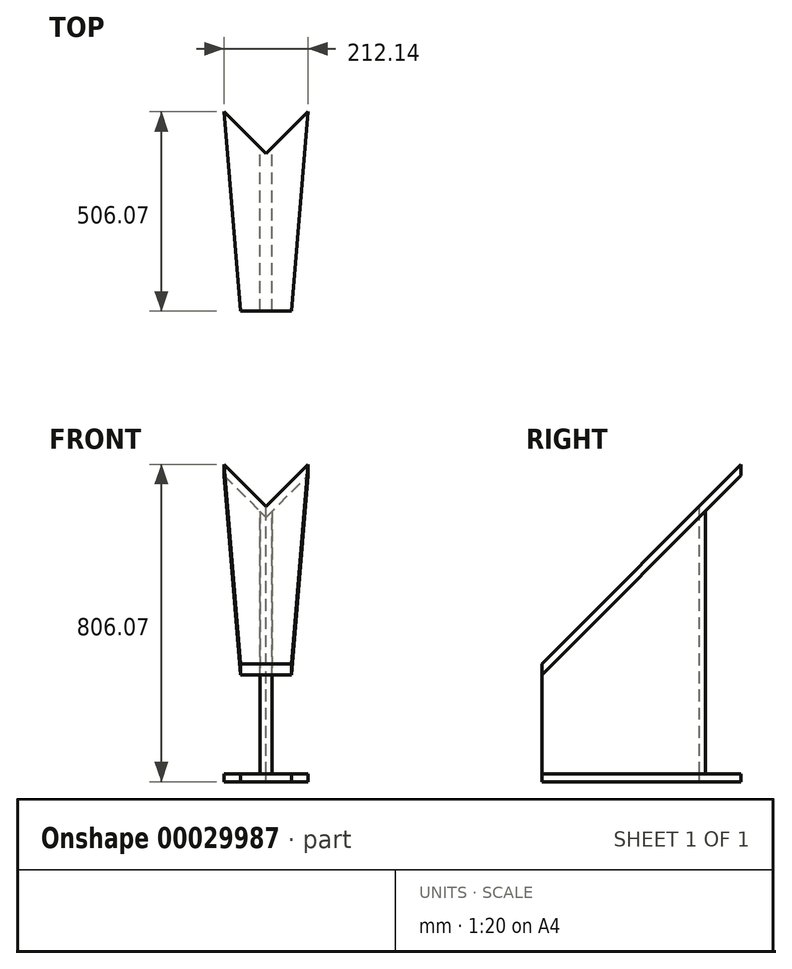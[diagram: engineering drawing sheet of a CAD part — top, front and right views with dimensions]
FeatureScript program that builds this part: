
annotation { "Feature Type Name" : "Feature", "Feature Type Description" : "" }
export const myFeature = defineFeature(function(context is Context, id is Id, definition is map)
    precondition{}
    {
        {
            var Q0;
            Q0=qCreatedBy(makeId("Right.planeOp"),FACE);
            var sketch = newSketch(context, id + "F0", { "sketchPlane" : qUnion([Q0])});
            skLineSegment(sketch, "E0", {"start": v(0, 569.29) * mm, "end": v(0, 0) * mm, "construction": true});
            skLineSegment(sketch, "E1", {"start": v(0, 0) * mm, "end": v(899.87, 0) * mm, "construction": true});
            skLineSegment(sketch, "E2", {"start": v(0, 0) * mm, "end": v(-506.07, -506.07) * mm});
            skLineSegment(sketch, "E3", {"start": v(-506.07, -506.07) * mm, "end": v(-506.07, -534.35) * mm});
            skLineSegment(sketch, "E4", {"start": v(-506.07, -534.35) * mm, "end": v(0, -28.28) * mm});
            skLineSegment(sketch, "E5", {"start": v(0, -28.28) * mm, "end": v(0, 0) * mm});
            skLineSegment(sketch, "E6.bottom", {"start": v(-506.07, -786.07) * mm, "end": v(0, -786.07) * mm});
            skLineSegment(sketch, "E6.top", {"start": v(-506.07, -806.07) * mm, "end": v(0, -806.07) * mm});
            skLineSegment(sketch, "E6.left", {"start": v(-506.07, -786.07) * mm, "end": v(-506.07, -806.07) * mm});
            skLineSegment(sketch, "E6.right", {"start": v(0, -786.07) * mm, "end": v(0, -806.07) * mm});
            skSolve(sketch);
        }
        {
            var Q0;
            Q0=makeQuery(id+"F0.imprint","IMPRINT",FACE,{"disambiguationData":[TD([[makeQuery(id+"F0.imprint","IMPRINT",EDGE,{"derivedFrom":sQuery(id+"F0.wireOp",EDGE,"E2")}),1.0]])]});
            var Q1;
            Q1=makeQuery(id+"F0.imprint","IMPRINT",FACE,{"disambiguationData":[TD([[makeQuery(id+"F0.imprint","IMPRINT",EDGE,{"derivedFrom":sQuery(id+"F0.wireOp",EDGE,"E6.bottom")}),-1.0]])]});
            extrude(context, id + "F1", {"entities" : qUnion([Q0, Q1]), "endBound" : BoundingType.SYMMETRIC, "depth" : 212.13 * mm});
        }
        {
            var Q0;
            Q0=qCreatedBy(makeId("Right.planeOp"),FACE);
            var sketch = newSketch(context, id + "F2", { "sketchPlane" : qUnion([Q0])});
            skLineSegment(sketch, "E7", {"start": v(-506.07, -534.35) * mm, "end": v(0, -28.28) * mm});
            skLineSegment(sketch, "E8", {"start": v(0, -28.28) * mm, "end": v(0, -786.07) * mm});
            skLineSegment(sketch, "E9", {"start": v(0, -786.07) * mm, "end": v(-506.07, -786.07) * mm});
            skLineSegment(sketch, "E10", {"start": v(-506.07, -786.07) * mm, "end": v(-506.07, -534.35) * mm});
            skSolve(sketch);
        }
        {
            var Q0;
            Q0 = qSketchRegion(id + "F2", true);
            extrude(context, id + "F3", {"entities" : qUnion([Q0]), "endBound" : BoundingType.SYMMETRIC, "depth" : 30 * mm});
        }
        {
            var Q0;
            Q0=qCreatedBy(makeId("Top.planeOp"),FACE);
            var sketch = newSketch(context, id + "F4", { "sketchPlane" : qUnion([Q0])});
            skLineSegment(sketch, "E11", {"start": v(-106.07, 0) * mm, "end": v(-65, -506.07) * mm});
            skLineSegment(sketch, "E12", {"start": v(-65, -506.07) * mm, "end": v(-106.06, -506.07) * mm});
            skLineSegment(sketch, "E13", {"start": v(-106.06, -506.07) * mm, "end": v(-106.07, 0) * mm});
            skLineSegment(sketch, "E14", {"start": v(0, 0) * mm, "end": v(0, -561.47) * mm, "construction": true});
            skLineSegment(sketch, "E15", {"start": v(106.07, 0) * mm, "end": v(106.07, -506.07) * mm});
            skLineSegment(sketch, "E16", {"start": v(106.07, -506.07) * mm, "end": v(65, -506.07) * mm});
            skLineSegment(sketch, "E17", {"start": v(65, -506.07) * mm, "end": v(106.07, 0) * mm});
            skLineSegment(sketch, "E18", {"start": v(-106.07, 0) * mm, "end": v(106.07, 0) * mm});
            skLineSegment(sketch, "E19", {"start": v(-106.07, 0) * mm, "end": v(0, -106.07) * mm});
            skLineSegment(sketch, "E20", {"start": v(0, -106.07) * mm, "end": v(106.07, 0) * mm});
            skSolve(sketch);
        }
        {
            var Q0;
            Q0=makeQuery(id+"F4.imprint","IMPRINT",FACE,{"disambiguationData":[TD([[makeQuery(id+"F4.imprint","IMPRINT",EDGE,{"derivedFrom":sQuery(id+"F4.wireOp",EDGE,"E11")}),-1.0]])]});
            var Q1;
            Q1=makeQuery(id+"F4.imprint","IMPRINT",FACE,{"disambiguationData":[TD([[makeQuery(id+"F4.imprint","IMPRINT",EDGE,{"derivedFrom":sQuery(id+"F4.wireOp",EDGE,"E15")}),-1.0]])]});
            var Q2;
            Q2=makeQuery(id+"F4.imprint","IMPRINT",FACE,{"disambiguationData":[TD([[makeQuery(id+"F4.imprint","IMPRINT",EDGE,{"derivedFrom":sQuery(id+"F4.wireOp",EDGE,"E18")}),-1.0]])]});
            var Q3;
            Q3=makeQuery(id+"F1.opExtrude","SWEPT_FACE",FACE,{"disambiguationData":[OSD([sQuery(id+"F0.wireOp",EDGE,"E6.top")])]});
            extrude(context, id + "F5", {"entities" : qUnion([Q0, Q1, Q2]), "operationType" : NewBodyOperationType.REMOVE, "endBound" : BoundingType.UP_TO_SURFACE, "oppositeDirection" : true, "endBoundEntityFace" : qUnion([Q3]), "depth" : 25 * mm});
        }
    });
